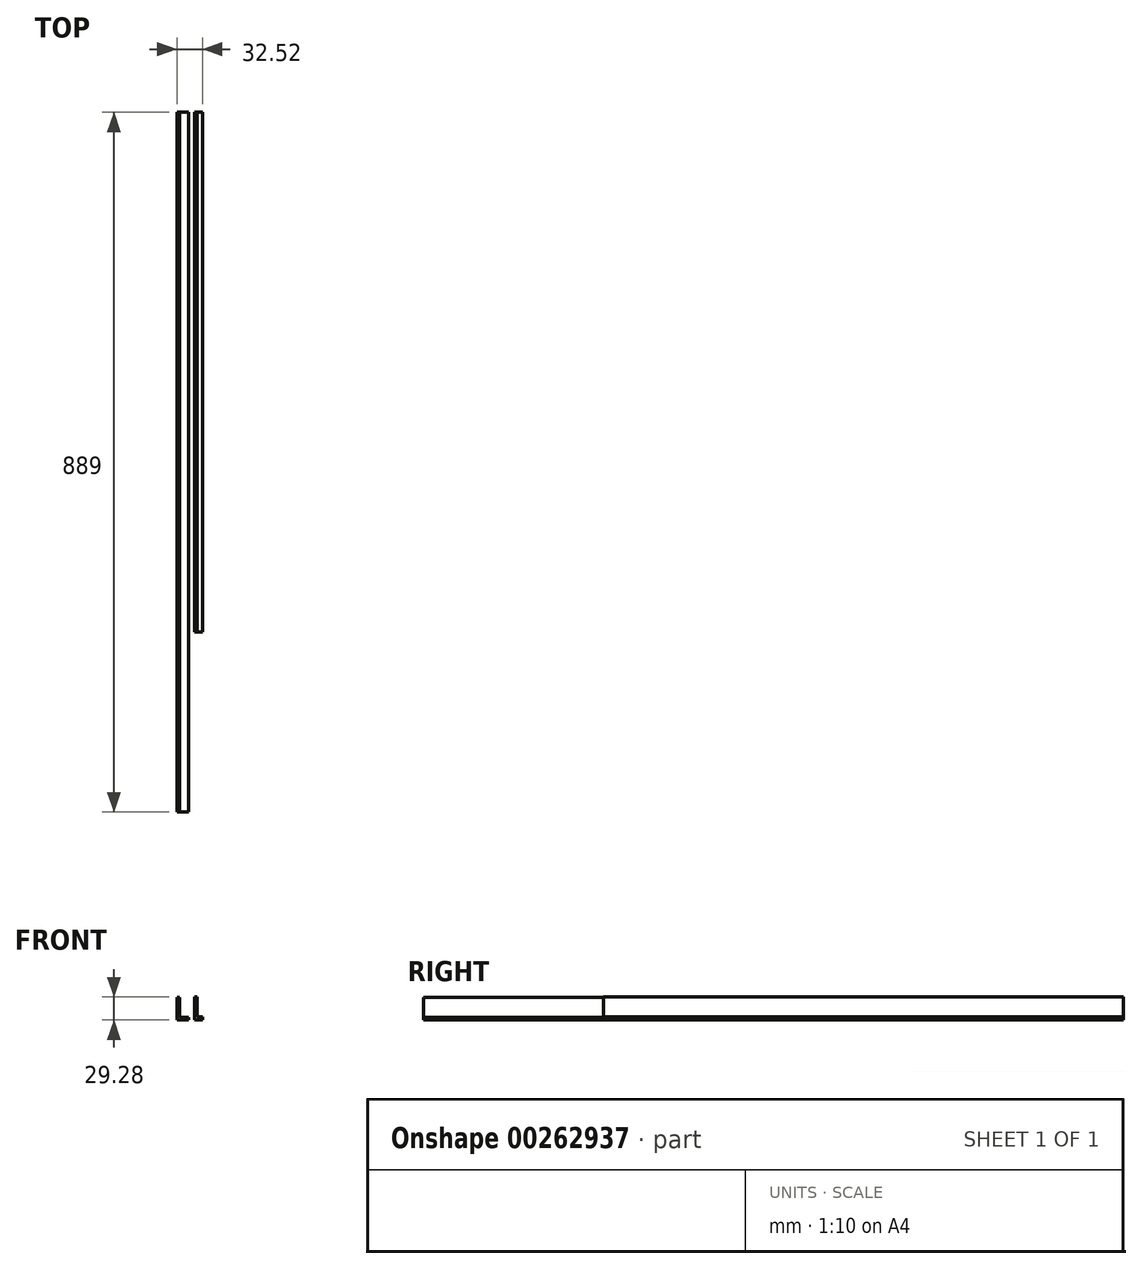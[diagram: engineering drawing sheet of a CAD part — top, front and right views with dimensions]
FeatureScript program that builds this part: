
annotation { "Feature Type Name" : "Feature", "Feature Type Description" : "" }
export const myFeature = defineFeature(function(context is Context, id is Id, definition is map)
    precondition{}
    {
        {
            var Q0;
            Q0=qCreatedBy(makeId("Front.planeOp"),FACE);
            var sketch = newSketch(context, id + "F0", { "sketchPlane" : qUnion([Q0])});
            skLineSegment(sketch, "E0", {"start": v(0, 0) * mm, "end": v(0, 28.89) * mm});
            skLineSegment(sketch, "E1", {"start": v(0, 28.89) * mm, "end": v(-3.53, 28.89) * mm});
            skLineSegment(sketch, "E2", {"start": v(-3.53, 28.89) * mm, "end": v(-3.53, 0) * mm});
            skLineSegment(sketch, "E3", {"start": v(-3.53, 0) * mm, "end": v(0, 0) * mm});
            skLineSegment(sketch, "E4", {"start": v(0, 0) * mm, "end": v(11.36, 0) * mm});
            skLineSegment(sketch, "E5", {"start": v(11.36, 0) * mm, "end": v(11.36, 3.3) * mm});
            skLineSegment(sketch, "E6", {"start": v(11.36, 3.3) * mm, "end": v(0, 3.3) * mm});
            skSolve(sketch);
        }
        {
            var Q0;
            Q0 = qSketchRegion(id + "F0", true);
            extrude(context, id + "F1", {"entities" : qUnion([Q0]), "depth" : 889 * mm});
        }
        {
            var Q0;
            Q0=qCreatedBy(makeId("Front.planeOp"),FACE);
            var sketch = newSketch(context, id + "F2", { "sketchPlane" : qUnion([Q0])});
            skLineSegment(sketch, "E7", {"start": v(18.6, 0) * mm, "end": v(18.6, 29.28) * mm});
            skLineSegment(sketch, "E8", {"start": v(18.6, 29.28) * mm, "end": v(22.13, 29.28) * mm});
            skLineSegment(sketch, "E9", {"start": v(22.13, 29.28) * mm, "end": v(22.13, 3.82) * mm});
            skLineSegment(sketch, "E10", {"start": v(22.13, 3.82) * mm, "end": v(28.99, 3.82) * mm});
            skLineSegment(sketch, "E11", {"start": v(28.99, 3.82) * mm, "end": v(28.99, 0) * mm});
            skLineSegment(sketch, "E12", {"start": v(28.99, 0) * mm, "end": v(18.6, 0) * mm});
            skSolve(sketch);
        }
        {
            var Q0;
            Q0=makeQuery(id+"F2.imprint","IMPRINT",FACE,{"disambiguationData":[TD([[makeQuery(id+"F2.imprint","IMPRINT",EDGE,{"derivedFrom":sQuery(id+"F2.wireOp",EDGE,"E7")}),-1.0]])]});
            extrude(context, id + "F3", {"entities" : qUnion([Q0]), "depth" : 660.4 * mm});
        }
    });
